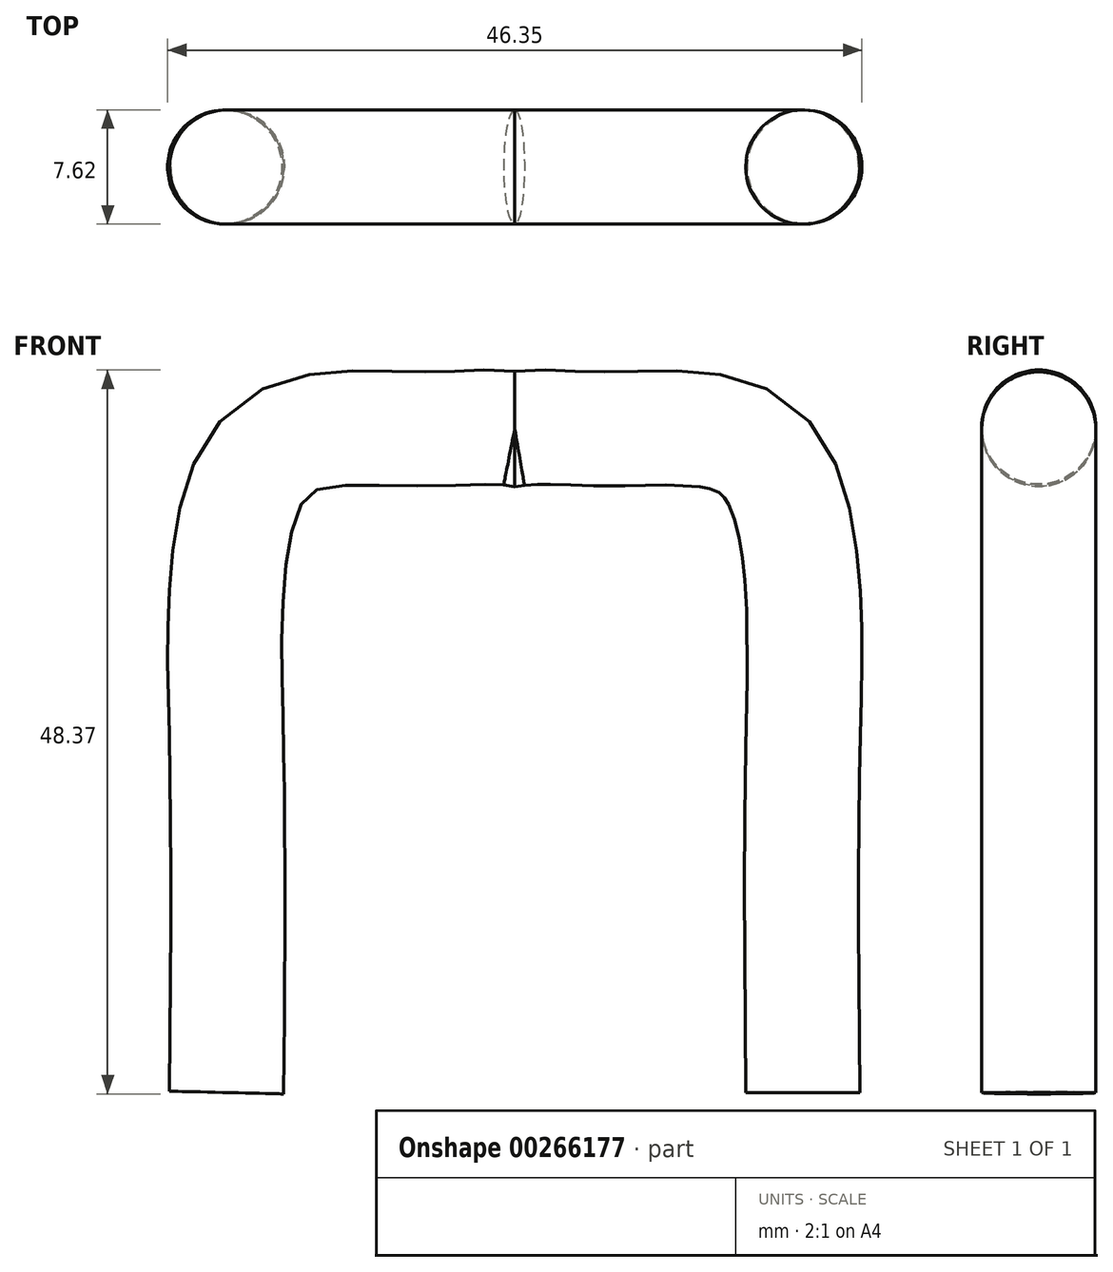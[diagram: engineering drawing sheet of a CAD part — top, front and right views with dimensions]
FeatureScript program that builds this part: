
annotation { "Feature Type Name" : "Feature", "Feature Type Description" : "" }
export const myFeature = defineFeature(function(context is Context, id is Id, definition is map)
    precondition{}
    {
        {
            var Q0;
            Q0=qCreatedBy(makeId("Top.planeOp"),FACE);
            var sketch = newSketch(context, id + "F0", { "sketchPlane" : qUnion([Q0])});
            skCircle(sketch, "E0", {"center": v(0, 0) * mm, "radius": 3.81 * mm});
            skSolve(sketch);
        }
        {
            var Q0;
            Q0=qCreatedBy(makeId("Front.planeOp"),FACE);
            var sketch = newSketch(context, id + "F1", { "sketchPlane" : qUnion([Q0])});
            skFitSpline(sketch, "E1", {"points": [v(0, 0) * mm, v(0, 22.93) * mm, v(0, 33.63) * mm, v(-3.19, 43.06) * mm, v(-12.87, 44.34) * mm, v(-19.24, 44.34) * mm], "startDerivative": vector(-1.02, 85.9) * mm, "endDerivative": vector(-31.55, -5.84) * mm});
            skFitSpline(sketch, "E2.MirrorCS", {"points": [v(-38.48, 0) * mm, v(-38.48, 22.93) * mm, v(-38.48, 33.63) * mm, v(-35.3, 43.06) * mm, v(-25.6, 44.34) * mm, v(-19.24, 44.34) * mm], "startDerivative": vector(1.02, 85.9) * mm, "endDerivative": vector(31.55, -5.84) * mm});
            skSolve(sketch);
        }
        {
            var Q0;
            Q0=makeQuery(id+"F0.imprint","IMPRINT",FACE,{"disambiguationData":[TD([[makeQuery(id+"F0.imprint","IMPRINT",EDGE,{"derivedFrom":sQuery(id+"F0.wireOp",EDGE,"E0")}),1.0]])]});
            var Q1;
            Q1=sQuery(id+"F1.wireOp",EDGE,"E1");
            var Q2;
            Q2=sQuery(id+"F1.wireOp",EDGE,"E2.MirrorCS");
            sweep(context, id + "F2", {"profiles" : qUnion([Q0]), "path" : qUnion([Q1, Q2])});
        }
    });
